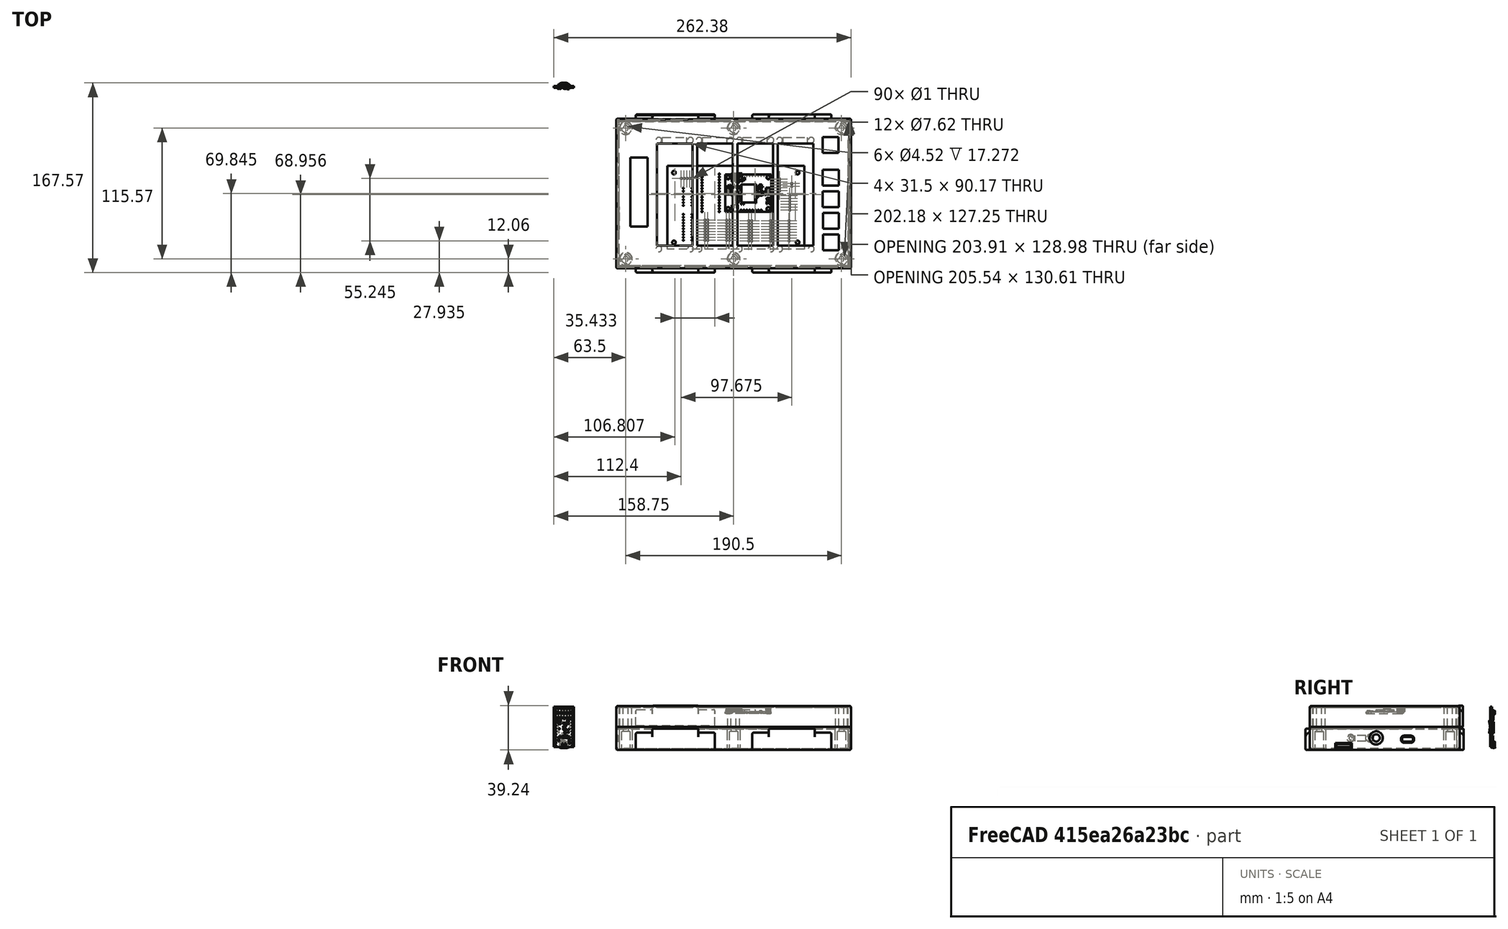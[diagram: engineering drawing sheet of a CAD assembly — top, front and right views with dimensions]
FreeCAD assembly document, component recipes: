
FREECAD ASSEMBLY — COMPONENT RECIPES ("case")

This assembly document has 3 components, labeled P0..P2 below (a component is one placed body or linked part). 0 of them carry a construction recipe — the FreeCAD feature program that regenerates the part from scratch, quoted from this document or its linked companion documents; the rest are supplied as boundary geometry only. No exploded tour is included for this assembly.
COMPONENT P0 — geometry summary ("race_computer_proto"; no construction recipe available for this part):
  bounding box: 121.2 x 73.5 x 18.1 mm
  tessellated surface: 91,328 triangles
  volume: 17714 mm^3 (11% of its bounding box)
COMPONENT P1 — geometry summary ("Link002(*Fillet002)"; no construction recipe available for this part):
  bounding box: 69.9 x 18.9 x 5.1 mm
  tessellated surface: 5,948 triangles
  volume: 4613 mm^3 (69% of its bounding box)
  symmetry: mirror-symmetric across its x mid-plane
COMPONENT P2 — geometry summary ("Link003(*Fillet002)"; no construction recipe available for this part):
  bounding box: 69.8 x 18.9 x 5.1 mm
  tessellated surface: 5,948 triangles
  volume: 4613 mm^3 (69% of its bounding box)
  symmetry: mirror-symmetric across its x mid-plane
PROVENANCE & LICENSES
A FreeCAD (.FCStd) document from a public repository crawl; recipes are the document's own serialized feature recipes (and, for linked parts, companion documents' recipes).
License: as declared in the source repository (recorded in the dataset sidecar).
